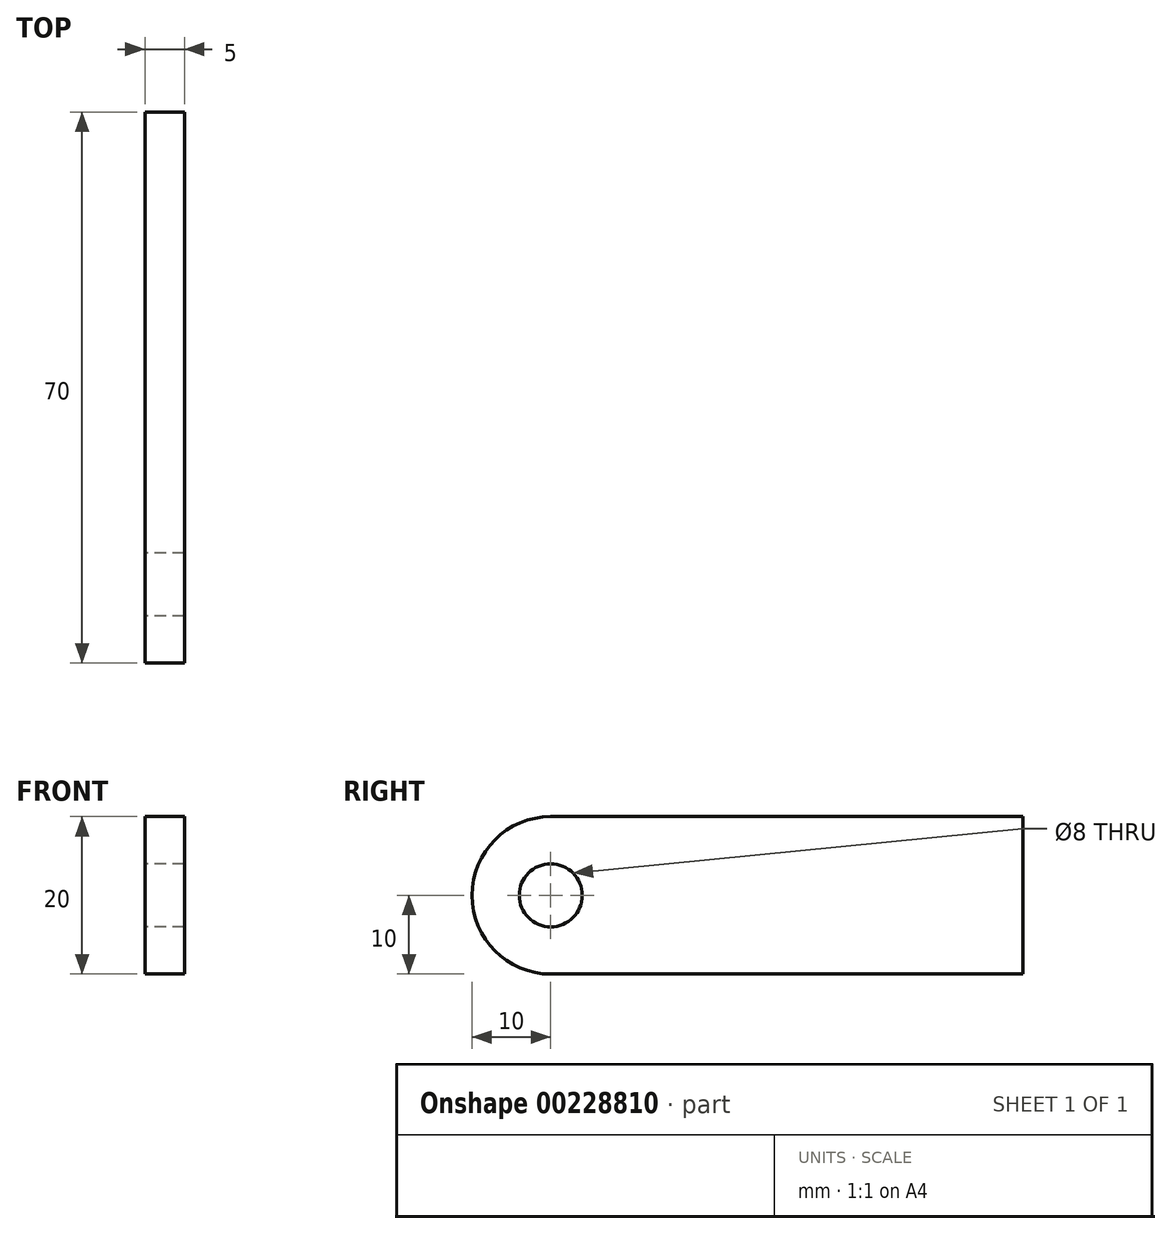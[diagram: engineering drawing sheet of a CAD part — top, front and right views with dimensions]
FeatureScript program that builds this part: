
annotation { "Feature Type Name" : "Feature", "Feature Type Description" : "" }
export const myFeature = defineFeature(function(context is Context, id is Id, definition is map)
    precondition{}
    {
        {
            var Q0;
            Q0=qCreatedBy(makeId("Top.planeOp"),FACE);
            var sketch = newSketch(context, id + "F0", { "sketchPlane" : qUnion([Q0])});
            skLineSegment(sketch, "E0.bottom", {"start": v(-2.5, 70) * mm, "end": v(2.5, 70) * mm});
            skLineSegment(sketch, "E0.top", {"start": v(-2.5, 0) * mm, "end": v(2.5, 0) * mm});
            skLineSegment(sketch, "E0.left", {"start": v(-2.5, 70) * mm, "end": v(-2.5, 0) * mm});
            skLineSegment(sketch, "E0.right", {"start": v(2.5, 70) * mm, "end": v(2.5, 0) * mm});
            skSolve(sketch);
        }
        {
            var Q0;
            Q0=makeQuery(id+"F0.imprint","IMPRINT",FACE,{"disambiguationData":[TD([[makeQuery(id+"F0.imprint","IMPRINT",EDGE,{"derivedFrom":sQuery(id+"F0.wireOp",EDGE,"E0.bottom")}),-1.0]])]});
            extrude(context, id + "F1", {"entities" : qUnion([Q0]), "depth" : 10 * mm, "hasSecondDirection" : true, "secondDirectionOppositeDirection" : true, "secondDirectionDepth" : 10 * mm});
        }
        {
            var Q0;
            Q0=makeQuery(id+"F1.opExtrude","CAP_EDGE",EDGE,{"disambiguationData":[OSD([sQuery(id+"F0.wireOp",EDGE,"E0.top")])],"isStart":false});
            var Q1;
            Q1=makeQuery(id+"F1.opExtrude","CAP_EDGE",EDGE,{"disambiguationData":[OSD([sQuery(id+"F0.wireOp",EDGE,"E0.top")])],"isStart":true});
            fillet(context, id + "F2", {"entities" : qUnion([Q0, Q1]), "radius" : 10 * mm, "tangentPropagation" : true, "allowEdgeOverflow" : false});
        }
        {
            var Q0;
            Q0=makeQuery(id+"F1.opExtrude","SWEPT_FACE",FACE,{"disambiguationData":[OSD([sQuery(id+"F0.wireOp",EDGE,"E0.left")])]});
            var sketch = newSketch(context, id + "F3", { "sketchPlane" : qUnion([Q0])});
            skCircle(sketch, "E1", {"center": v(-10, 0) * mm, "radius": 4 * mm});
            skSolve(sketch);
        }
        {
            var Q0;
            Q0=makeQuery(id+"F3.imprint","IMPRINT",FACE,{"disambiguationData":[TD([[makeQuery(id+"F3.imprint","IMPRINT",EDGE,{"derivedFrom":sQuery(id+"F3.wireOp",EDGE,"E1")}),1.0]])]});
            extrude(context, id + "F4", {"entities" : qUnion([Q0]), "operationType" : NewBodyOperationType.REMOVE, "endBound" : BoundingType.THROUGH_ALL, "oppositeDirection" : true, "depth" : 25 * mm});
        }
    });
